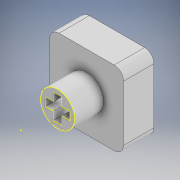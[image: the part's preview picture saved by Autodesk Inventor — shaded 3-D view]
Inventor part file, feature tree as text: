
AUTODESK INVENTOR PART (.ipt)
format: ipt  version: 2022 (Build 260153000, 153)  size: 237,056 bytes
history: native  units: in
note: dims shown in document units (in); Inventor stores cm internally (conversion verified against a paired STEP export)
features: sketch x5, extrude x3, projected_geometry x2, plane x1
ambient origin geometry x8: Origin, YZ Plane, XZ Plane, XY Plane, X Axis, Y Axis, Z Axis, Center Point
bodies: Body1 (feature_tree)
feature tree (11):
  sketch  "Sketch1"  dims[d3=0.2205in d4=0.1594in]
  plane  "Work Plane1"
  sketch  "Sketch2"  dims[d5=0.0531in d6=0.1594in]
  extrude  "Extrusion3"  Depth=0.1594in
  extrude  "Extrusion4"  Depth=0.1594in
  extrude  "Extrusion5"  Depth=0.5016in
  sketch  "Sketch5"  dims[d14=0.2205in d15=0.1594in d16=0.0531in d17=0.1594in d18=0.0531in d19=0.189in d20=0.0in d21=0.0892in d22=0.2693in d23=0.0354in d24=0.0in]
  projected_geometry  "Projected Loop1"
  sketch  "Sketch3"  dims[d7=0.0531in d10=0.5016in]
  sketch  "Sketch4"  dims[d12=0.1969in d13=0.0in]
  projected_geometry  "Projected Loop2"
